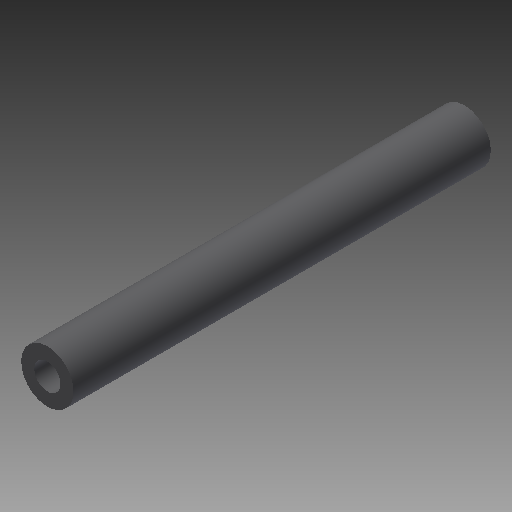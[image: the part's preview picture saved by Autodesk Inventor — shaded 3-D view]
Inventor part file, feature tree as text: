
AUTODESK INVENTOR PART (.ipt)
format: ipt  version: 2017 (Build 210142000, 142)  size: 98,304 bytes
history: native  units: in
note: dims shown in document units (in); Inventor stores cm internally (conversion verified against a paired STEP export)
features: other x7, sketch x2, revolve x1, hole x1
ambient origin geometry x8: Origin, YZ Plane, XZ Plane, XY Plane, X Axis, Y Axis, Z Axis, Center Point
bodies: Solid1 (feature_tree)
feature tree (11):
  revolve  "Revolution1"  [1 undecoded]
  hole  "Hole1"  [1 undecoded]
  other  "screw_XY"
  other  "screw_YZ"
  other  "screw_ZX"
  other  "screw_X"
  other  "screw_Y"
  other  "screw_Z"
  other  "screw_Center"
  sketch  "Sketch_1"  dims[d0=360.0deg]
  sketch  "Sketch2"  dims[d1=0.118in d2=0.75in d3=0.375in d4=0.25in d5=0.5635in d6=1.872in d7=0.0in d8=0.0in]
note: 2 required parameter values undecoded (feature->parameter linkage not recoverable at this tier; creation-order binding heuristic only, values carry confidence <= 0.55)